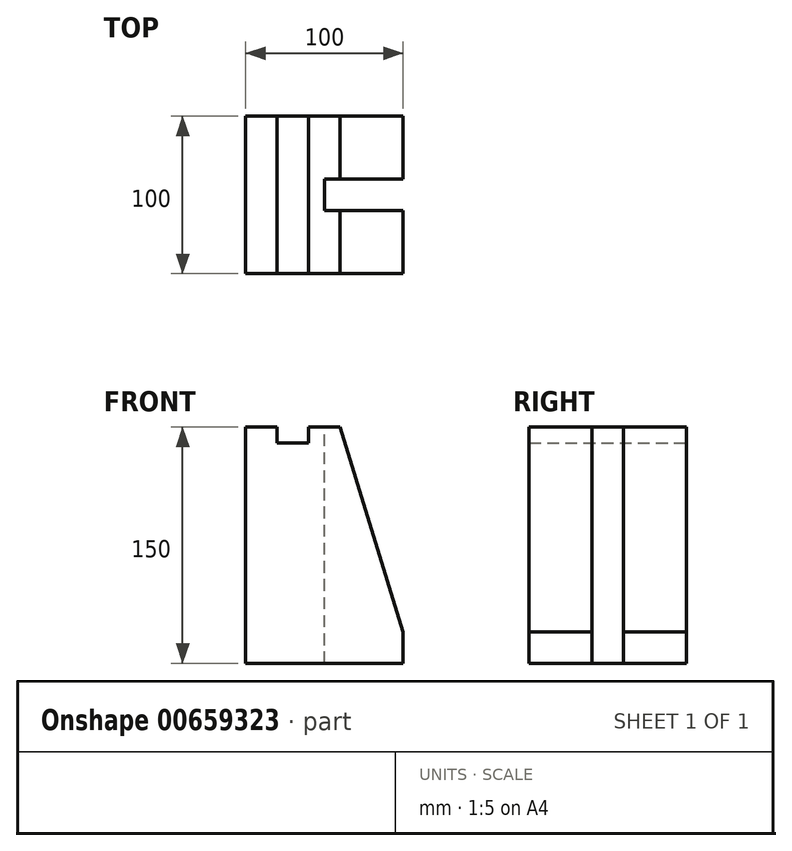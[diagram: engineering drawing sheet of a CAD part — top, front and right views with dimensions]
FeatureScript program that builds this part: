
annotation { "Feature Type Name" : "Feature", "Feature Type Description" : "" }
export const myFeature = defineFeature(function(context is Context, id is Id, definition is map)
    precondition{}
    {
        {
            var Q0;
            Q0=qCreatedBy(makeId("Front.planeOp"),FACE);
            var sketch = newSketch(context, id + "F0", { "sketchPlane" : qUnion([Q0])});
            skLineSegment(sketch, "E0", {"start": v(0, 0) * mm, "end": v(100, 0) * mm});
            skLineSegment(sketch, "E1", {"start": v(100, 0) * mm, "end": v(0, 0) * mm});
            skLineSegment(sketch, "E2", {"start": v(0, 0) * mm, "end": v(0, 150) * mm});
            skLineSegment(sketch, "E3", {"start": v(100, 0) * mm, "end": v(100, 20) * mm});
            skLineSegment(sketch, "E4", {"start": v(60, 150) * mm, "end": v(100, 20) * mm});
            skLineSegment(sketch, "E5", {"start": v(0, 150) * mm, "end": v(20, 150) * mm});
            skLineSegment(sketch, "E6", {"start": v(20, 150) * mm, "end": v(20, 140) * mm});
            skLineSegment(sketch, "E7", {"start": v(20, 140) * mm, "end": v(40, 140) * mm});
            skLineSegment(sketch, "E8", {"start": v(40, 140) * mm, "end": v(40, 150) * mm});
            skLineSegment(sketch, "E9", {"start": v(40, 150) * mm, "end": v(60, 150) * mm});
            skSolve(sketch);
        }
        {
            var Q0;
            Q0 = qSketchRegion(id + "F0", true);
            extrude(context, id + "F1", {"entities" : qUnion([Q0]), "depth" : 100 * mm, "offsetDistance" : 25 * mm});
        }
        {
            var Q0;
            Q0=makeQuery(id+"F1.opExtrude","SWEPT_FACE",FACE,{"disambiguationData":[OSD([sQuery(id+"F0.wireOp",EDGE,"E9")])]});
            var sketch = newSketch(context, id + "F2", { "sketchPlane" : qUnion([Q0])});
            skLineSegment(sketch, "E10", {"start": v(60, -40) * mm, "end": v(50, -40) * mm});
            skLineSegment(sketch, "E11", {"start": v(50, -40) * mm, "end": v(50, -60) * mm});
            skLineSegment(sketch, "E12", {"start": v(50, -60) * mm, "end": v(60, -60) * mm});
            skLineSegment(sketch, "E13.bottom", {"start": v(50, -40) * mm, "end": v(100, -40) * mm});
            skLineSegment(sketch, "E13.top", {"start": v(50, -60) * mm, "end": v(100, -60) * mm});
            skLineSegment(sketch, "E13.right", {"start": v(100, -40) * mm, "end": v(100, -60) * mm});
            skSolve(sketch);
        }
        {
            var Q0;
            {var subQ0=sQuery(id+"F2.wireOp",EDGE,"E11");Q0=makeQuery(id+"F2.imprint","IMPRINT",FACE,{"disambiguationData":[TD([[makeQuery(id+"F2.imprint","IMPRINT",EDGE,{"derivedFrom":subQ0}),1.0]])]});}
            var Q1;
            {var subQ0=sQuery(id+"F2.wireOp",EDGE,"E13.right");Q1=makeQuery(id+"F2.imprint","IMPRINT",FACE,{"disambiguationData":[TD([[makeQuery(id+"F2.imprint","IMPRINT",EDGE,{"derivedFrom":subQ0}),-1.0]])]});}
            extrude(context, id + "F3", {"entities" : qUnion([Q0, Q1]), "operationType" : NewBodyOperationType.REMOVE, "oppositeDirection" : true, "depth" : 150 * mm, "offsetDistance" : 25 * mm});
        }
    });
